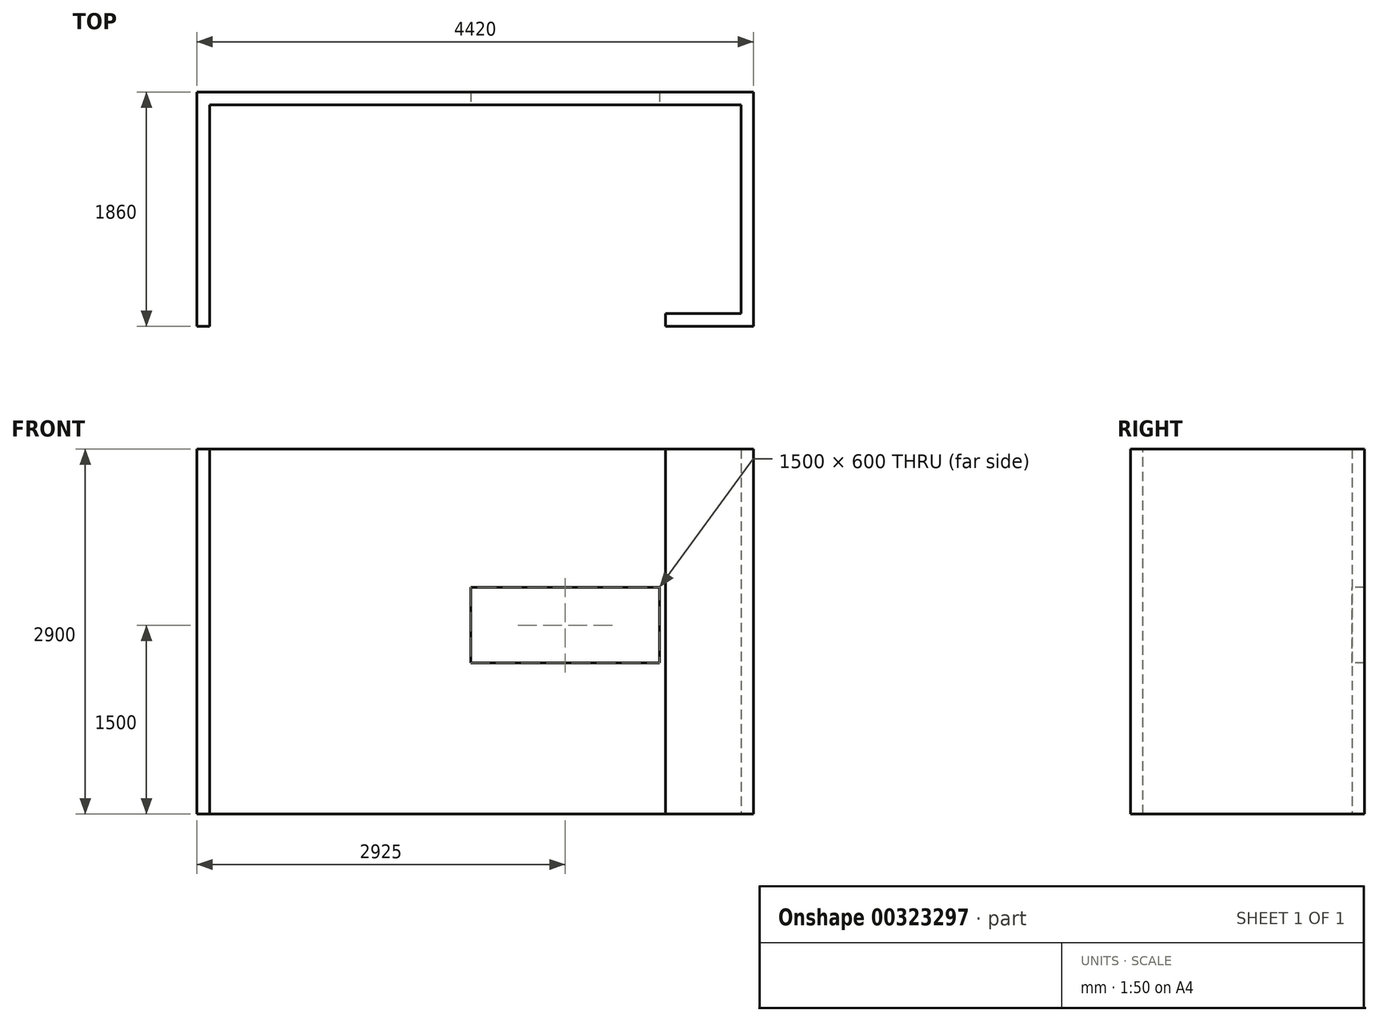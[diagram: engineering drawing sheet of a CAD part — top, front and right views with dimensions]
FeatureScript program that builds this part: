
annotation { "Feature Type Name" : "Feature", "Feature Type Description" : "" }
export const myFeature = defineFeature(function(context is Context, id is Id, definition is map)
    precondition{}
    {
        {
            var Q0;
            Q0=qCreatedBy(makeId("Top.planeOp"),FACE);
            var sketch = newSketch(context, id + "F0", { "sketchPlane" : qUnion([Q0])});
            skLineSegment(sketch, "E0", {"start": v(0, 0) * mm, "end": v(0, 1760) * mm});
            skLineSegment(sketch, "E1", {"start": v(0, 1760) * mm, "end": v(4220, 1760) * mm});
            skLineSegment(sketch, "E2", {"start": v(4220, 1760) * mm, "end": v(4220, 0) * mm});
            skLineSegment(sketch, "E3.0", {"start": v(-100, 1860) * mm, "end": v(4320, 1860) * mm});
            skLineSegment(sketch, "E4.0", {"start": v(-100, 0) * mm, "end": v(-100, 1860) * mm});
            skLineSegment(sketch, "E5.0", {"start": v(4320, 1860) * mm, "end": v(4320, 0) * mm});
            skLineSegment(sketch, "E6", {"start": v(0, 0) * mm, "end": v(-100, 0) * mm});
            skLineSegment(sketch, "E7", {"start": v(4220, 0) * mm, "end": v(4320, 0) * mm});
            skSolve(sketch);
        }
        {
            var Q0;
            Q0 = qSketchRegion(id + "F0", true);
            extrude(context, id + "F1", {"entities" : qUnion([Q0]), "depth" : 2900 * mm});
        }
        {
            var Q0;
            Q0=makeQuery(id+"F1.opExtrude","SWEPT_FACE",FACE,{"disambiguationData":[OSD([sQuery(id+"F0.wireOp",EDGE,"E1")])]});
            var sketch = newSketch(context, id + "F2", { "sketchPlane" : qUnion([Q0])});
            skLineSegment(sketch, "E8.bottom", {"start": v(2075, 1200) * mm, "end": v(3575, 1200) * mm});
            skLineSegment(sketch, "E8.top", {"start": v(2075, 1800) * mm, "end": v(3575, 1800) * mm});
            skLineSegment(sketch, "E8.left", {"start": v(2075, 1200) * mm, "end": v(2075, 1800) * mm});
            skLineSegment(sketch, "E8.right", {"start": v(3575, 1200) * mm, "end": v(3575, 1800) * mm});
            skSolve(sketch);
        }
        {
            var Q0;
            Q0 = qSketchRegion(id + "F2", true);
            extrude(context, id + "F3", {"entities" : qUnion([Q0]), "operationType" : NewBodyOperationType.REMOVE, "endBound" : BoundingType.UP_TO_NEXT, "oppositeDirection" : true, "depth" : 25 * mm});
        }
        {
            var Q0;
            Q0=makeQuery(id+"F1.opExtrude","CAP_FACE",FACE,{"disambiguationData":[OSD([sQuery(id+"F0.wireOp",EDGE,"E0"),sQuery(id+"F0.wireOp",EDGE,"E1"),sQuery(id+"F0.wireOp",EDGE,"E2"),sQuery(id+"F0.wireOp",EDGE,"E3.0"),sQuery(id+"F0.wireOp",EDGE,"E4.0"),sQuery(id+"F0.wireOp",EDGE,"E5.0"),sQuery(id+"F0.wireOp",EDGE,"E6"),sQuery(id+"F0.wireOp",EDGE,"E7")])],"isStart":false});
            var sketch = newSketch(context, id + "F4", { "sketchPlane" : qUnion([Q0])});
            skLineSegment(sketch, "E9.bottom", {"start": v(4320, 0) * mm, "end": v(3620, 0) * mm});
            skLineSegment(sketch, "E9.top", {"start": v(4320, 100) * mm, "end": v(3620, 100) * mm});
            skLineSegment(sketch, "E9.left", {"start": v(4320, 0) * mm, "end": v(4320, 100) * mm});
            skLineSegment(sketch, "E9.right", {"start": v(3620, 0) * mm, "end": v(3620, 100) * mm});
            skSolve(sketch);
        }
        {
            var Q0;
            Q0 = qSketchRegion(id + "F4", true);
            extrude(context, id + "F5", {"entities" : qUnion([Q0]), "operationType" : NewBodyOperationType.ADD, "oppositeDirection" : true, "depth" : 2900 * mm});
        }
    });
